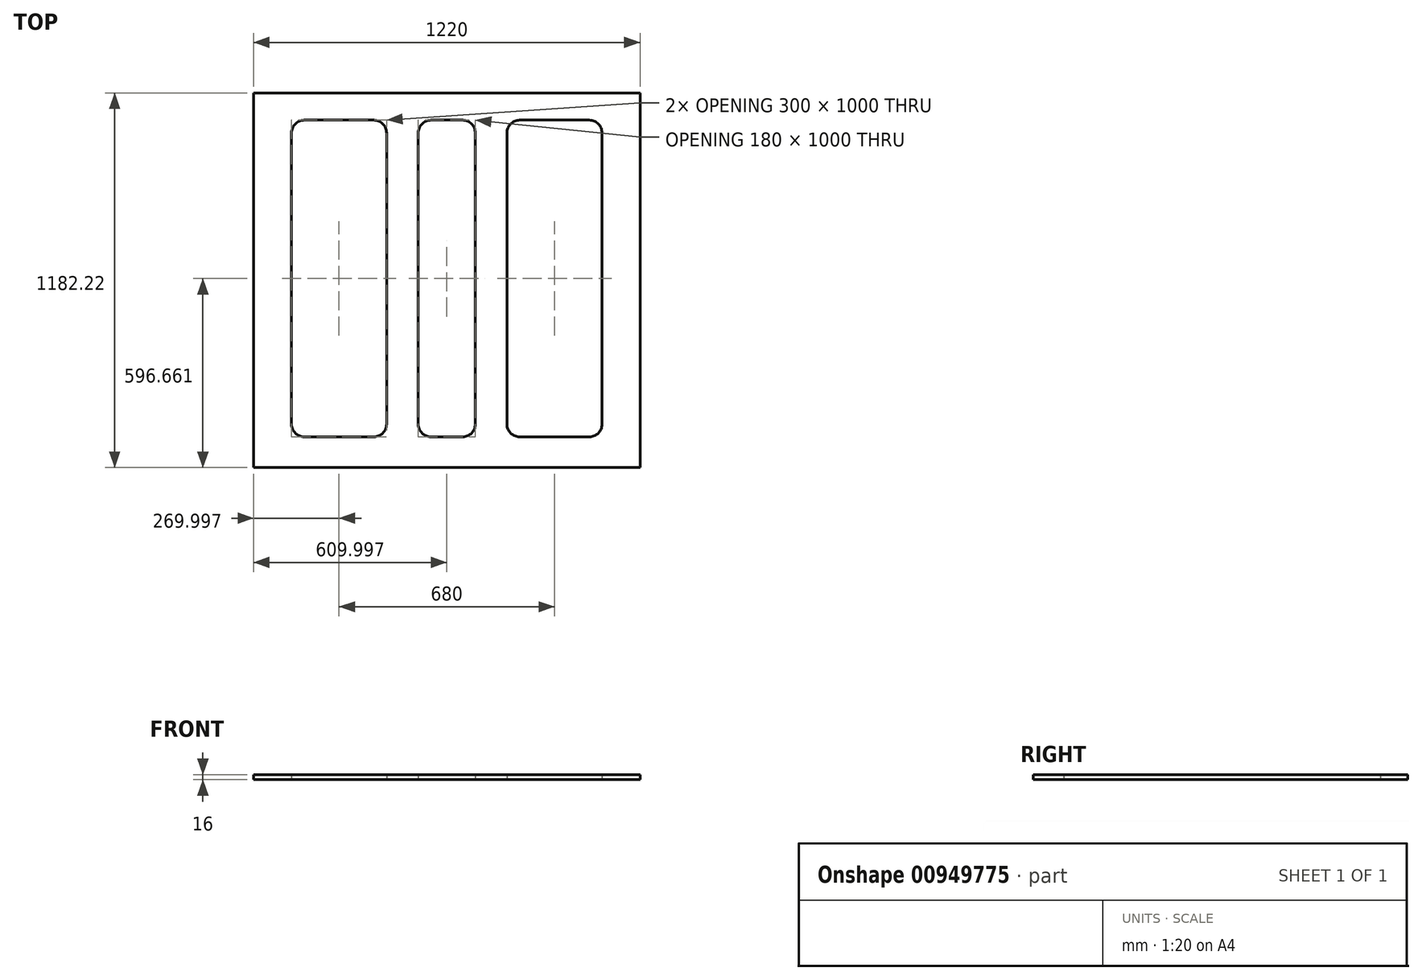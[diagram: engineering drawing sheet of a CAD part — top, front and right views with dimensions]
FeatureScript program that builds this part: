
annotation { "Feature Type Name" : "Feature", "Feature Type Description" : "" }
export const myFeature = defineFeature(function(context is Context, id is Id, definition is map)
    precondition{}
    {
        {
            var Q0;
            Q0=qCreatedBy(makeId("Top.planeOp"),FACE);
            var sketch = newSketch(context, id + "F0", { "sketchPlane" : qUnion([Q0])});
            skLineSegment(sketch, "E0.bottom", {"start": v(-563.9, -494.04) * mm, "end": v(656.1, -494.04) * mm});
            skLineSegment(sketch, "E0.top", {"start": v(-563.9, 705.96) * mm, "end": v(656.1, 705.96) * mm});
            skLineSegment(sketch, "E0.left", {"start": v(-563.9, -494.04) * mm, "end": v(-563.9, 705.96) * mm});
            skLineSegment(sketch, "E0.right", {"start": v(656.1, -494.04) * mm, "end": v(656.1, 705.96) * mm});
            skSolve(sketch);
        }
        {
            var Q0;
            Q0=makeQuery(id+"F0.imprint","IMPRINT",FACE,{"disambiguationData":[TD([[makeQuery(id+"F0.imprint","IMPRINT",EDGE,{"derivedFrom":sQuery(id+"F0.wireOp",EDGE,"E0.bottom")}),1.0]])]});
            var sketch = newSketch(context, id + "F1", { "sketchPlane" : qUnion([Q0])});
            skLineSegment(sketch, "E1.bottom", {"start": v(-403.9, 605.96) * mm, "end": v(-183.9, 605.96) * mm});
            skLineSegment(sketch, "E1.top", {"start": v(-403.9, -394.04) * mm, "end": v(-183.9, -394.04) * mm});
            skLineSegment(sketch, "E1.left", {"start": v(-443.9, 565.96) * mm, "end": v(-443.9, -354.04) * mm});
            skLineSegment(sketch, "E1.right", {"start": v(-143.9, 565.96) * mm, "end": v(-143.9, -354.04) * mm});
            skLineSegment(sketch, "E2.bottom", {"start": v(-3.9, 605.96) * mm, "end": v(96.1, 605.96) * mm});
            skLineSegment(sketch, "E2.top", {"start": v(-3.9, -394.04) * mm, "end": v(96.1, -394.04) * mm});
            skLineSegment(sketch, "E2.left", {"start": v(-43.9, 565.96) * mm, "end": v(-43.9, -354.04) * mm});
            skLineSegment(sketch, "E2.right", {"start": v(136.1, 565.96) * mm, "end": v(136.1, -354.04) * mm});
            skLineSegment(sketch, "E3.bottom", {"start": v(276.1, -394.04) * mm, "end": v(496.1, -394.04) * mm});
            skLineSegment(sketch, "E3.top", {"start": v(276.1, 605.96) * mm, "end": v(496.1, 605.96) * mm});
            skLineSegment(sketch, "E3.left", {"start": v(236.1, -354.04) * mm, "end": v(236.1, 565.96) * mm});
            skLineSegment(sketch, "E3.right", {"start": v(536.1, -354.04) * mm, "end": v(536.1, 565.96) * mm});
            skPoint(sketch, "E4.visualSharp", {"position": v(-443.9, 605.96) * mm});
            skArc(sketch, "E4.filletArc", {"start": v(-403.9, 605.96) * mm, "mid": v(-432.18, 594.25) * mm, "end": v(-443.9, 565.96) * mm});
            skPoint(sketch, "E5.visualSharp", {"position": v(-143.9, 605.96) * mm});
            skArc(sketch, "E5.filletArc", {"start": v(-143.9, 565.96) * mm, "mid": v(-155.6, 594.25) * mm, "end": v(-183.9, 605.96) * mm});
            skPoint(sketch, "E6.visualSharp", {"position": v(-443.9, -394.04) * mm});
            skArc(sketch, "E6.filletArc", {"start": v(-443.9, -354.04) * mm, "mid": v(-432.18, -382.32) * mm, "end": v(-403.9, -394.04) * mm});
            skPoint(sketch, "E7.visualSharp", {"position": v(-143.9, -394.04) * mm});
            skArc(sketch, "E7.filletArc", {"start": v(-183.9, -394.04) * mm, "mid": v(-155.6, -382.32) * mm, "end": v(-143.9, -354.04) * mm});
            skPoint(sketch, "E8.visualSharp", {"position": v(-43.9, -394.04) * mm});
            skArc(sketch, "E8.filletArc", {"start": v(-43.9, -354.04) * mm, "mid": v(-32.18, -382.32) * mm, "end": v(-3.9, -394.04) * mm});
            skPoint(sketch, "E9.visualSharp", {"position": v(136.1, -394.04) * mm});
            skArc(sketch, "E9.filletArc", {"start": v(96.1, -394.04) * mm, "mid": v(124.4, -382.32) * mm, "end": v(136.1, -354.04) * mm});
            skPoint(sketch, "E10.visualSharp", {"position": v(-43.9, 605.96) * mm});
            skArc(sketch, "E10.filletArc", {"start": v(-3.9, 605.96) * mm, "mid": v(-32.18, 594.25) * mm, "end": v(-43.9, 565.96) * mm});
            skPoint(sketch, "E11.visualSharp", {"position": v(136.1, 605.96) * mm});
            skArc(sketch, "E11.filletArc", {"start": v(136.1, 565.96) * mm, "mid": v(124.4, 594.25) * mm, "end": v(96.1, 605.96) * mm});
            skPoint(sketch, "E12.visualSharp", {"position": v(236.1, 605.96) * mm});
            skArc(sketch, "E12.filletArc", {"start": v(276.1, 605.96) * mm, "mid": v(247.82, 594.25) * mm, "end": v(236.1, 565.96) * mm});
            skPoint(sketch, "E13.visualSharp", {"position": v(536.1, 605.96) * mm});
            skArc(sketch, "E13.filletArc", {"start": v(536.1, 565.96) * mm, "mid": v(524.4, 594.25) * mm, "end": v(496.1, 605.96) * mm});
            skPoint(sketch, "E14.visualSharp", {"position": v(536.1, -394.04) * mm});
            skArc(sketch, "E14.filletArc", {"start": v(496.1, -394.04) * mm, "mid": v(524.4, -382.32) * mm, "end": v(536.1, -354.04) * mm});
            skPoint(sketch, "E15.visualSharp", {"position": v(236.1, -394.04) * mm});
            skArc(sketch, "E15.filletArc", {"start": v(236.1, -354.04) * mm, "mid": v(247.82, -382.32) * mm, "end": v(276.1, -394.04) * mm});
            skLineSegment(sketch, "E16.bottom", {"start": v(-563.9, -490.7) * mm, "end": v(656.1, -490.7) * mm});
            skLineSegment(sketch, "E16.top", {"start": v(-563.9, 691.52) * mm, "end": v(656.1, 691.52) * mm});
            skLineSegment(sketch, "E16.left", {"start": v(-563.9, -490.7) * mm, "end": v(-563.9, 691.52) * mm});
            skLineSegment(sketch, "E16.right", {"start": v(656.1, -490.7) * mm, "end": v(656.1, 691.52) * mm});
            skSolve(sketch);
        }
        {
            var Q0;
            Q0=makeQuery(id+"F1.imprint","IMPRINT",FACE,{"disambiguationData":[TD([[makeQuery(id+"F1.imprint","IMPRINT",EDGE,{"derivedFrom":sQuery(id+"F1.wireOp",EDGE,"E1.bottom")}),1.0]])]});
            var sketch = newSketch(context, id + "F2", { "sketchPlane" : qUnion([Q0])});
            skSolve(sketch);
        }
        {
            var Q0;
            Q0=makeQuery(id+"F2.imprint","IMPRINT",FACE,{"disambiguationData":[TD([[makeQuery(id+"F2.imprint","IMPRINT",EDGE,{"derivedFrom":makeQuery(id+"F1.imprint","IMPRINT",EDGE,{"derivedFrom":sQuery(id+"F1.wireOp",EDGE,"E1.bottom")})}),1.0]])]});
            extrude(context, id + "F3", {"entities" : qUnion([Q0]), "depth" : 16 * mm, "offsetDistance" : 25 * mm});
        }
    });
